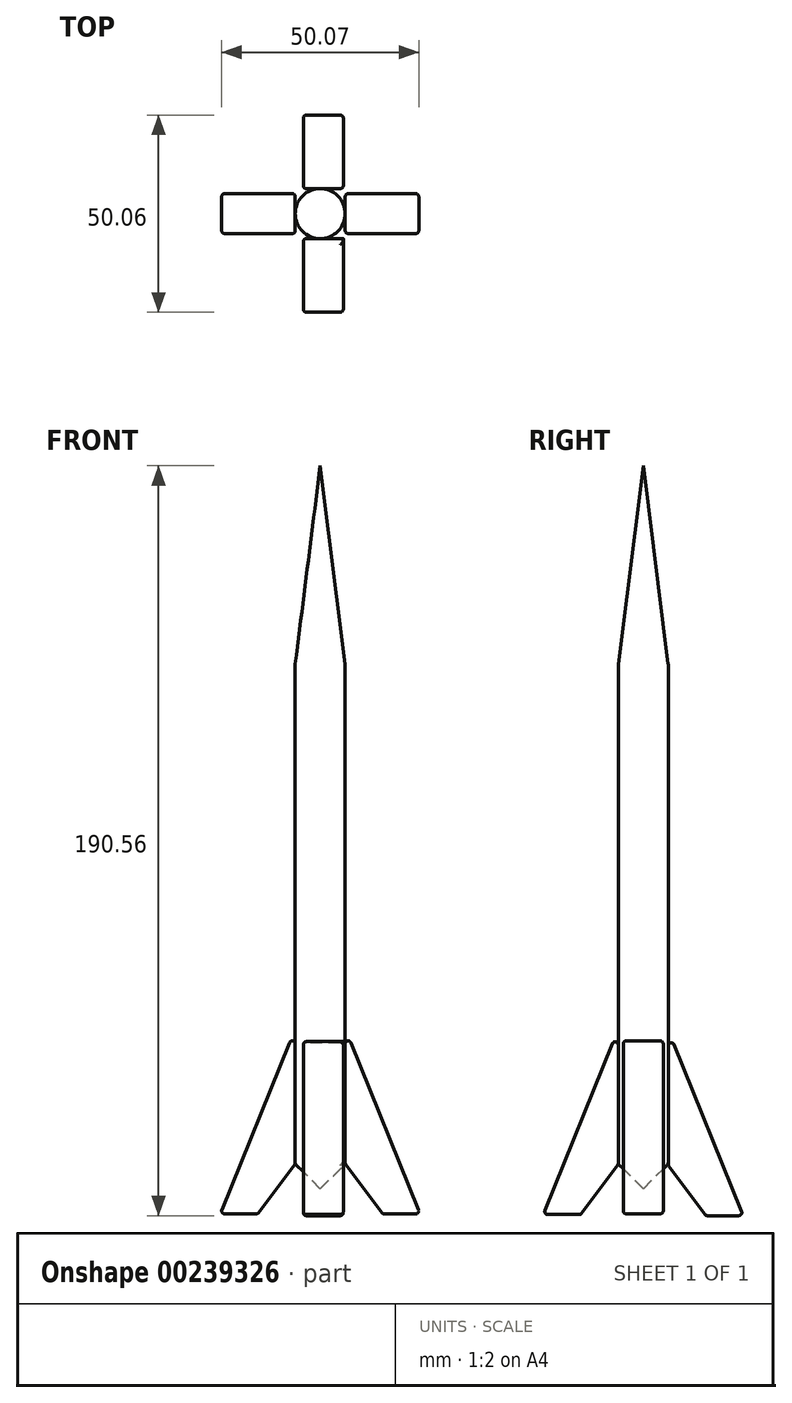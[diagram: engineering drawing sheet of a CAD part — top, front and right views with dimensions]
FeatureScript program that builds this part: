
annotation { "Feature Type Name" : "Feature", "Feature Type Description" : "" }
export const myFeature = defineFeature(function(context is Context, id is Id, definition is map)
    precondition{}
    {
        {
            var Q0;
            Q0=qCreatedBy(makeId("Front.planeOp"),FACE);
            var sketch = newSketch(context, id + "F0", { "sketchPlane" : qUnion([Q0])});
            skLineSegment(sketch, "E0", {"start": v(-7.13, -62.24) * mm, "end": v(-7.13, 64.76) * mm});
            skLineSegment(sketch, "E1", {"start": v(5.57, -62.24) * mm, "end": v(5.57, 64.76) * mm});
            skLineSegment(sketch, "E2", {"start": v(-7.13, 64.76) * mm, "end": v(5.57, 64.76) * mm});
            skLineSegment(sketch, "E3", {"start": v(-7.13, -62.24) * mm, "end": v(5.57, -62.24) * mm});
            skLineSegment(sketch, "E4", {"start": v(-0.78, 64.76) * mm, "end": v(-0.78, -62.24) * mm});
            skSolve(sketch);
        }
        {
            var Q0;
            {var subQ0=sQuery(id+"F0.wireOp",EDGE,"E1");Q0=makeQuery(id+"F0.imprint","IMPRINT",FACE,{"disambiguationData":[TD([[makeQuery(id+"F0.imprint","IMPRINT",EDGE,{"derivedFrom":subQ0}),1.0]])]});}
            var Q1;
            Q1=sQuery(id+"F0.wireOp",EDGE,"E4");
            var Q2;
            Q2=sQuery(id+"F0.wireOp",EDGE,"E4");
            revolve(context, id + "F1", {"entities" : qUnion([Q0]), "surfaceEntities" : qUnion([Q1]), "axis" : qUnion([Q2]), "revolveType" : RevolveType.FULL});
        }
        {
            var Q0;
            Q0=qCreatedBy(makeId("Front.planeOp"),FACE);
            var sketch = newSketch(context, id + "F2", { "sketchPlane" : qUnion([Q0])});
            skLineSegment(sketch, "E5.0", {"start": v(-7.13, -62.24) * mm, "end": v(5.57, -62.24) * mm});
            skLineSegment(sketch, "E6", {"start": v(5.57, 64.76) * mm, "end": v(5.57, -62.24) * mm});
            skLineSegment(sketch, "E7", {"start": v(-7.13, -62.24) * mm, "end": v(-7.13, 64.76) * mm});
            skLineSegment(sketch, "E8", {"start": v(-26.18, -74.94) * mm, "end": v(-7.13, -27.84) * mm});
            skLineSegment(sketch, "E9", {"start": v(5.57, -27.84) * mm, "end": v(24.62, -74.94) * mm});
            skLineSegment(sketch, "E10", {"start": v(-7.13, -62.24) * mm, "end": v(-16.66, -74.94) * mm});
            skLineSegment(sketch, "E11", {"start": v(5.57, -62.24) * mm, "end": v(15.1, -74.94) * mm});
            skLineSegment(sketch, "E12", {"start": v(24.62, -74.94) * mm, "end": v(15.1, -74.94) * mm});
            skLineSegment(sketch, "E13", {"start": v(-16.66, -74.94) * mm, "end": v(-26.18, -74.94) * mm});
            skSolve(sketch);
        }
        {
            var Q0;
            Q0 = qSketchRegion(id + "F2", true);
            extrude(context, id + "F3", {"entities" : qUnion([Q0]), "operationType" : NewBodyOperationType.ADD, "endBound" : BoundingType.SYMMETRIC, "depth" : 10.16 * mm});
        }
        {
            var Q0;
            Q0=qCreatedBy(makeId("Right.planeOp"),FACE);
            var sketch = newSketch(context, id + "F4", { "sketchPlane" : qUnion([Q0])});
            skLineSegment(sketch, "E14", {"start": v(6.35, 64.76) * mm, "end": v(6.35, -62.7) * mm});
            skLineSegment(sketch, "E15", {"start": v(-6.35, -62.43) * mm, "end": v(-6.35, 64.76) * mm});
            skLineSegment(sketch, "E16", {"start": v(-25.4, -75.13) * mm, "end": v(-6.35, -28.04) * mm});
            skLineSegment(sketch, "E17", {"start": v(25.4, -75.4) * mm, "end": v(6.35, -28.3) * mm});
            skLineSegment(sketch, "E18", {"start": v(6.35, -62.7) * mm, "end": v(15.88, -75.4) * mm});
            skLineSegment(sketch, "E19", {"start": v(-6.35, -62.43) * mm, "end": v(-15.88, -75.13) * mm});
            skLineSegment(sketch, "E20", {"start": v(25.4, -75.4) * mm, "end": v(15.88, -75.4) * mm});
            skLineSegment(sketch, "E21", {"start": v(-15.88, -75.13) * mm, "end": v(-25.4, -75.13) * mm});
            skSolve(sketch);
        }
        {
            var Q0;
            Q0 = qSketchRegion(id + "F4", true);
            extrude(context, id + "F5", {"entities" : qUnion([Q0]), "operationType" : NewBodyOperationType.ADD, "endBound" : BoundingType.SYMMETRIC, "depth" : 10.16 * mm});
        }
        {
            var Q0;
            Q0=qCreatedBy(makeId("Front.planeOp"),FACE);
            var sketch = newSketch(context, id + "F6", { "sketchPlane" : qUnion([Q0])});
            skLineSegment(sketch, "E22.0", {"start": v(-7.13, 64.76) * mm, "end": v(5.57, 64.76) * mm});
            skLineSegment(sketch, "E23", {"start": v(-7.13, 64.76) * mm, "end": v(-0.78, 115.16) * mm});
            skPoint(sketch, "E23.endSnap0", {"position": v(-0.78, 64.76) * mm});
            skLineSegment(sketch, "E24", {"start": v(-0.78, 64.76) * mm, "end": v(-0.78, 115.16) * mm});
            skSolve(sketch);
        }
        {
            var Q0;
            Q0 = qSketchRegion(id + "F6", true);
            var Q1;
            Q1=sQuery(id+"F6.wireOp",EDGE,"E24");
            revolve(context, id + "F7", {"operationType" : NewBodyOperationType.ADD, "entities" : qUnion([Q0]), "axis" : qUnion([Q1]), "revolveType" : RevolveType.FULL});
        }
        {
            var Q0;
            Q0=qCreatedBy(makeId("Front.planeOp"),FACE);
            var sketch = newSketch(context, id + "F8", { "sketchPlane" : qUnion([Q0])});
            skLineSegment(sketch, "E25.0", {"start": v(-7.13, -62.24) * mm, "end": v(5.57, -62.24) * mm});
            skLineSegment(sketch, "E26", {"start": v(-7.13, -62.24) * mm, "end": v(-0.78, -68.59) * mm});
            skPoint(sketch, "E26.endSnap0", {"position": v(-0.78, -62.24) * mm});
            skLineSegment(sketch, "E27", {"start": v(-0.78, -68.59) * mm, "end": v(-0.78, -62.24) * mm});
            skSolve(sketch);
        }
        {
            var Q0;
            Q0 = qSketchRegion(id + "F8", true);
            var Q1;
            Q1=sQuery(id+"F8.wireOp",EDGE,"E27");
            revolve(context, id + "F9", {"operationType" : NewBodyOperationType.ADD, "entities" : qUnion([Q0]), "axis" : qUnion([Q1]), "revolveType" : RevolveType.FULL});
        }
        {
            var Q0;
            Q0=makeQuery(id+"F5.opExtrude","SWEPT_FACE",FACE,{"disambiguationData":[OSD([sQuery(id+"F4.wireOp",EDGE,"E16")])]});
            var Q1;
            Q1=makeQuery(id+"F5.opExtrude","CAP_FACE",FACE,{"disambiguationData":[OSD([sQuery(id+"F4.wireOp",EDGE,"E15"),sQuery(id+"F4.wireOp",EDGE,"E16"),sQuery(id+"F4.wireOp",EDGE,"E19"),sQuery(id+"F4.wireOp",EDGE,"E21")])],"isStart":true});
            var Q2;
            Q2=makeQuery(id+"F3.opExtrude","CAP_FACE",FACE,{"disambiguationData":[OSD([sQuery(id+"F2.wireOp",EDGE,"E7"),sQuery(id+"F2.wireOp",EDGE,"E8"),sQuery(id+"F2.wireOp",EDGE,"E10"),sQuery(id+"F2.wireOp",EDGE,"E13")])],"isStart":false});
            var Q3;
            Q3=makeQuery(id+"F3.opExtrude","SWEPT_FACE",FACE,{"disambiguationData":[OSD([sQuery(id+"F2.wireOp",EDGE,"E8")])]});
            var Q4;
            Q4=makeQuery(id+"F3.opExtrude","CAP_FACE",FACE,{"disambiguationData":[OSD([sQuery(id+"F2.wireOp",EDGE,"E7"),sQuery(id+"F2.wireOp",EDGE,"E8"),sQuery(id+"F2.wireOp",EDGE,"E10"),sQuery(id+"F2.wireOp",EDGE,"E13")])],"isStart":true});
            var Q5;
            Q5=makeQuery(id+"F5.opExtrude","CAP_FACE",FACE,{"disambiguationData":[OSD([sQuery(id+"F4.wireOp",EDGE,"E14"),sQuery(id+"F4.wireOp",EDGE,"E17"),sQuery(id+"F4.wireOp",EDGE,"E18"),sQuery(id+"F4.wireOp",EDGE,"E20")])],"isStart":true});
            var Q6;
            Q6=makeQuery(id+"F5.opExtrude","SWEPT_FACE",FACE,{"disambiguationData":[OSD([sQuery(id+"F4.wireOp",EDGE,"E17")])]});
            var Q7;
            Q7=makeQuery(id+"F3.opExtrude","CAP_FACE",FACE,{"disambiguationData":[OSD([sQuery(id+"F2.wireOp",EDGE,"E6"),sQuery(id+"F2.wireOp",EDGE,"E9"),sQuery(id+"F2.wireOp",EDGE,"E11"),sQuery(id+"F2.wireOp",EDGE,"E12")])],"isStart":true});
            var Q8;
            Q8=makeQuery(id+"F3.opExtrude","SWEPT_FACE",FACE,{"disambiguationData":[OSD([sQuery(id+"F2.wireOp",EDGE,"E9")])]});
            var Q9;
            Q9=makeQuery(id+"F5.opExtrude","CAP_FACE",FACE,{"disambiguationData":[OSD([sQuery(id+"F4.wireOp",EDGE,"E14"),sQuery(id+"F4.wireOp",EDGE,"E17"),sQuery(id+"F4.wireOp",EDGE,"E18"),sQuery(id+"F4.wireOp",EDGE,"E20")])],"isStart":false});
            var Q10;
            Q10=makeQuery(id+"F3.opExtrude","CAP_FACE",FACE,{"disambiguationData":[OSD([sQuery(id+"F2.wireOp",EDGE,"E6"),sQuery(id+"F2.wireOp",EDGE,"E9"),sQuery(id+"F2.wireOp",EDGE,"E11"),sQuery(id+"F2.wireOp",EDGE,"E12")])],"isStart":false});
            var Q11;
            Q11=makeQuery(id+"F5.opExtrude","SWEPT_FACE",FACE,{"disambiguationData":[OSD([sQuery(id+"F4.wireOp",EDGE,"E19")])]});
            var Q12;
            Q12=makeQuery(id+"F5.opExtrude","SWEPT_FACE",FACE,{"disambiguationData":[OSD([sQuery(id+"F4.wireOp",EDGE,"E21")])]});
            var Q13;
            Q13=makeQuery(id+"F3.opExtrude","SWEPT_FACE",FACE,{"disambiguationData":[OSD([sQuery(id+"F2.wireOp",EDGE,"E12")])]});
            var Q14;
            Q14=makeQuery(id+"F3.opExtrude","SWEPT_EDGE",EDGE,{"disambiguationData":[OSD([sQuery(id+"F2.wireOp",EDGE,"E6"),sQuery(id+"F2.wireOp",EDGE,"E11")])]});
            var Q15;
            Q15=makeQuery(id+"F5.opExtrude","SWEPT_FACE",FACE,{"disambiguationData":[OSD([sQuery(id+"F4.wireOp",EDGE,"E18")])]});
            var Q16;
            Q16=makeQuery(id+"F5.opExtrude","SWEPT_FACE",FACE,{"disambiguationData":[OSD([sQuery(id+"F4.wireOp",EDGE,"E20")])]});
            var Q17;
            Q17=makeQuery(id+"F3.opExtrude","SWEPT_FACE",FACE,{"disambiguationData":[OSD([sQuery(id+"F2.wireOp",EDGE,"E10")])]});
            var Q18;
            Q18=makeQuery(id+"F3.opExtrude","SWEPT_FACE",FACE,{"disambiguationData":[OSD([sQuery(id+"F2.wireOp",EDGE,"E13")])]});
            fillet(context, id + "F10", {"entities" : qUnion([Q0, Q1, Q2, Q3, Q4, Q5, Q6, Q7, Q8, Q9, Q10, Q11, Q12, Q13, Q14, Q15, Q16, Q17, Q18]), "radius" : 0.76 * mm, "tangentPropagation" : true, "allowEdgeOverflow" : false});
        }
        {
            var Q0;
            Q0=makeQuery(id+"F7.boolean.opBoolean","MERGE",EDGE,{"derivedFrom":[makeQuery(id+"F1.opRevolve","SWEPT_EDGE",EDGE,{"disambiguationData":[OSD([sQuery(id+"F0.wireOp",EDGE,"E1"),sQuery(id+"F0.wireOp",EDGE,"E2")])]}),makeQuery(id+"F7.opRevolve","SWEPT_EDGE",EDGE,{"disambiguationData":[OSD([sQuery(id+"F6.wireOp",EDGE,"E22.0"),sQuery(id+"F6.wireOp",EDGE,"E23")])]})]});
            var Q1;
            Q1=makeQuery(id+"F9.boolean.opBoolean","MERGE",EDGE,{"derivedFrom":[makeQuery(id+"F1.opRevolve","SWEPT_EDGE",EDGE,{"disambiguationData":[OSD([sQuery(id+"F0.wireOp",EDGE,"E1"),sQuery(id+"F0.wireOp",EDGE,"E3")])]}),makeQuery(id+"F9.opRevolve","SWEPT_EDGE",EDGE,{"disambiguationData":[OSD([sQuery(id+"F8.wireOp",EDGE,"E25.0"),sQuery(id+"F8.wireOp",EDGE,"E26")])]})]});
            fillet(context, id + "F11", {"entities" : qUnion([Q0, Q1]), "radius" : 0.76 * mm, "tangentPropagation" : true, "allowEdgeOverflow" : false});
        }
    });
